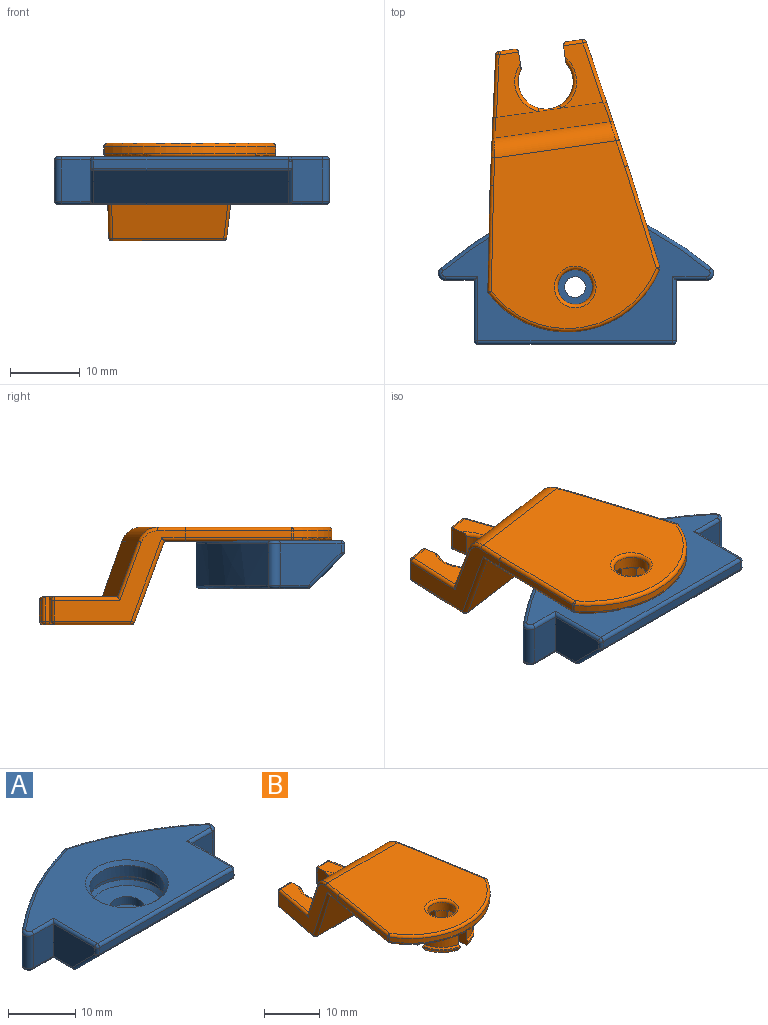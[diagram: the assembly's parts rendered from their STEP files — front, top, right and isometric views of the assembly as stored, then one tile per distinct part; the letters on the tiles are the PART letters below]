
ASSEMBLY  parts=2 mates=1
PART A: 51 faces, bbox 40.5x21.6x6.9 mm
  f0: cylinder r=2.5mm len=5mm, axis (0,0,1), area 22mm2, adj f12,f46
  f1: cylinder r=1.5mm len=3mm, axis (0,0,-1), area 8.5mm2, adj f12,f44
  f2: plane 8.72x5.9mm, normal (1,0,0), area 40.4mm2, adj f3,f23,f28,f34,f39
  f3: plane 5.9x4.38mm, normal (0,-1,0), area 25.8mm2, adj f2,f13,f21,f41
  f4: extruded ~19.54x10.36mm, area 131.4mm2, adj f5,f13,f17,f42
  f5: extruded ~19.28x10.34mm, area 130.1mm2, adj f4,f14,f15,f40
  f6: plane 5.9x4.15mm, normal (0,-1,0), area 24.5mm2, adj f7,f14,f18,f36
  f7: plane 8.72x5.9mm, normal (-1,0,0), area 40.4mm2, adj f6,f20,f25,f30,f33
  f8: plane 28x1.19mm, normal (0,-1,0), area 33.4mm2, adj f29,f30,f34,f35
  f9: plane 38.53x20.32mm, normal (0,0,1), area 401.7mm2, adj f33,f35,f36,f38,f39,f40,f41,f42
  f10: plane 38.53x15.61mm, normal (0,0,-1), area 376.2mm2, adj f15,f16,f17,f18,f19,f20,f21,f23
  f11: plane 28x4.71mm, normal (0,-0.71,-0.71), area 186.4mm2, adj f24,f25,f28,f29
  f12: plane 5x5mm, normal (0,0,1), area 12.6mm2, adj f0,f1
  f13: cylinder r=1mm len=5.9mm, axis (0,0,-1), area 14.3mm2, adj f3,f4,f19,f43
  f14: cylinder r=1mm len=5.9mm, axis (0,0,-1), area 14.5mm2, adj f5,f6,f16,f38
  f15: bspline ~20.66x11.54mm, area 17.2mm2, adj f5,f10,f16,f17
  f16: torus R=0.5mm, axis (0,0,1), area 1.6mm2, adj f10,f14,f15,f18
  f17: bspline ~21.54x11.77mm, area 17.4mm2, adj f4,f10,f15,f19
  f18: cylinder r=0.5mm len=4.65mm, axis (1,0,0), area 3.5mm2, adj f6,f10,f16,f20
  f19: torus R=0.5mm, axis (0,0,1), area 1.6mm2, adj f10,f13,f17,f21
  f20: cylinder r=0.5mm len=4.51mm, axis (0,-1,0), area 3.3mm2, adj f7,f10,f18,f22
  f21: cylinder r=0.5mm len=4.88mm, axis (1,0,0), area 3.6mm2, adj f3,f10,f19,f23
  f22: sphere r=0.5mm, area 0.1mm2, adj f20,f24,f25
  f23: cylinder r=0.5mm len=4.51mm, axis (0,1,0), area 3.3mm2, adj f2,f10,f21,f26
  f24: cylinder r=0.5mm len=28mm, axis (1,0,0), area 11mm2, adj f10,f11,f22,f26
  f25: cylinder r=0.5mm len=5.06mm, axis (0,-0.71,0.71), area 5.2mm2, adj f7,f11,f22,f27
  f26: sphere r=0.5mm, area 0.2mm2, adj f23,f24,f28
  f27: sphere r=0.5mm, area 0.2mm2, adj f25,f29,f30
  f28: cylinder r=0.5mm len=5.06mm, axis (0,0.71,-0.71), area 5.2mm2, adj f2,f11,f26,f31
  f29: cylinder r=0.5mm len=28mm, axis (1,0,0), area 11mm2, adj f8,f11,f27,f31
  f30: cylinder r=0.5mm len=1.19mm, axis (0,0,-1), area 0.9mm2, adj f7,f8,f27,f32
  f31: sphere r=0.5mm, area 0.2mm2, adj f28,f29,f34
  f32: sphere r=0.5mm, area 0.4mm2, adj f30,f33,f35
  f33: cylinder r=0.5mm len=9.22mm, axis (0,1,0), area 7mm2, adj f7,f9,f32,f36
  f34: cylinder r=0.5mm len=1.19mm, axis (0,0,-1), area 0.9mm2, adj f2,f8,f31,f37
  f35: cylinder r=0.5mm len=28mm, axis (-1,0,0), area 22mm2, adj f8,f9,f32,f37
  f36: cylinder r=0.5mm len=4.65mm, axis (-1,0,0), area 3.5mm2, adj f6,f9,f33,f38
  f37: sphere r=0.5mm, area 0.5mm2, adj f34,f35,f39
  f38: torus R=0.5mm, axis (0,0,1), area 1.6mm2, adj f9,f14,f36,f40
  f39: cylinder r=0.5mm len=9.22mm, axis (0,-1,0), area 7mm2, adj f2,f9,f37,f41
  f40: bspline ~20.66x11.54mm, area 17.2mm2, adj f5,f9,f38,f42
  f41: cylinder r=0.5mm len=4.88mm, axis (-1,0,0), area 3.6mm2, adj f3,f9,f39,f43
  f42: bspline ~21.54x11.77mm, area 17.4mm2, adj f4,f9,f40,f43
  f43: torus R=0.5mm, axis (0,0,1), area 1.6mm2, adj f9,f13,f41,f42
  f44: torus R=2mm, axis (0,0,1), area 8.3mm2, adj f1,f10
  f45: cylinder r=5.55mm len=11.1mm, axis (0,0,1), area 69.7mm2, adj f49,f50
  f46: plane 10.7x10.7mm, normal (0,0,1), area 70.3mm2, adj f0,f48
  f47: cylinder r=5.85mm len=11.7mm, axis (0,0,1), area 17.9mm2, adj f48,f49
  f48: cone r=5.35mm half-angle=35deg, axis (0,0,1), area 30.7mm2, adj f46,f47
  f49: cone r=5.85mm half-angle=45deg, axis (0,0,-1), area 15.2mm2, adj f45,f47
  f50: cone r=5.55mm half-angle=45deg, axis (0,0,1), area 31.2mm2, adj f9,f45
PART B: 124 faces, bbox 27x42.8x14.2 mm
  f0: plane 3.44x1mm, normal (0,0,-1), area 3.4mm2, adj f13,f58,f62,f93
  f1: plane 8.86x6.05mm, normal (0,0,1), area 28.1mm2, adj f44,f49,f69,f71,f120
  f2: plane 24.89x23.96mm, normal (0,0,-1), area 393.8mm2, adj f13,f50,f51,f53,f54,f55,f57,f59
  f3: plane 18.45x13mm, normal (0.98,0.18,0), area 64.3mm2, adj f69,f70,f72,f73,f77,f79,f80,f82
  f4: plane 18.45x13mm, normal (-0.98,0.18,0), area 64.3mm2, adj f98,f99,f105,f110,f113,f116,f117,f118
  f5: plane 25.86x23.96mm, normal (0,0,1), area 483.9mm2, adj f67,f82,f91,f102,f112,f117,f123
  f6: cylinder r=5.5mm len=4.41mm, axis (0,0,1), area 14.6mm2, adj f26,f27,f35,f60
  f7: cylinder r=5.5mm len=4.41mm, axis (0,0,1), area 14.6mm2, adj f22,f23,f37,f57
  f8: cylinder r=5.5mm len=4.41mm, axis (0,0,1), area 14.6mm2, adj f18,f20,f36,f53
  f9: cylinder r=5.5mm len=4.41mm, axis (0,0,1), area 14.6mm2, adj f15,f16,f34,f63
  f10: plane 15.07x2.47mm, normal (-0.99,0.16,0), area 15.3mm2, adj f103,f104,f112,f113
  f11: cylinder r=14.31mm len=24.82mm, axis (0,0,-1), area 30mm2, adj f92,f93,f102,f103
  f12: plane 15.07x2.47mm, normal (0.99,0.16,0), area 15.3mm2, adj f83,f84,f91,f92
  f13: cylinder r=2.5mm len=5mm, axis (0,0,-1), area 26.2mm2, adj f0,f2,f51,f52,f54,f55,f56,f58
  f14: cylinder r=2.75mm len=3.5mm, axis (0,0,1), area 8mm2, adj f15,f16,f17,f66
  f15: plane 3.5x3.16mm, normal (0,-1,0), area 10.1mm2, adj f9,f14,f17,f30,f34,f39,f64
  f16: plane 3.5x3.16mm, normal (-1,0,0), area 10.1mm2, adj f9,f14,f17,f30,f34,f39,f65
  f17: plane 4.21x4.21mm, normal (0,0,-1), area 11mm2, adj f14,f15,f16,f39
  f18: plane 3.5x3.16mm, normal (0,-1,0), area 10.1mm2, adj f8,f19,f21,f31,f36,f41,f51
  f19: cylinder r=2.75mm len=3.5mm, axis (0,0,1), area 8mm2, adj f18,f20,f21,f52
  f20: plane 3.5x3.16mm, normal (1,0,0), area 10.1mm2, adj f8,f19,f21,f31,f36,f41,f54
  f21: plane 4.21x4.21mm, normal (0,0,-1), area 11mm2, adj f18,f19,f20,f41
  f22: plane 3.5x3.16mm, normal (0,1,0), area 10.1mm2, adj f7,f24,f25,f32,f37,f40,f55
  f23: plane 3.5x3.16mm, normal (1,0,0), area 10.1mm2, adj f7,f24,f25,f32,f37,f40,f58
  f24: cylinder r=2.75mm len=3.5mm, axis (0,0,1), area 8mm2, adj f22,f23,f25,f56
  f25: plane 4.21x4.21mm, normal (0,0,-1), area 11mm2, adj f22,f23,f24,f40
  f26: plane 3.5x3.16mm, normal (-1,0,0), area 10.1mm2, adj f6,f28,f29,f33,f35,f38,f62
  f27: plane 3.5x3.16mm, normal (0,1,0), area 10.1mm2, adj f6,f28,f29,f33,f35,f38,f59
  f28: cylinder r=2.75mm len=3.5mm, axis (0,0,1), area 8mm2, adj f26,f27,f29,f61
  f29: plane 4.21x4.21mm, normal (0,0,-1), area 11mm2, adj f26,f27,f28,f38
  f30: cylinder r=5.8mm len=4.71mm, axis (0,0,1), area 2mm2, adj f15,f16,f34,f39
  f31: cylinder r=5.8mm len=4.71mm, axis (0,0,1), area 2mm2, adj f18,f20,f36,f41
  f32: cylinder r=5.8mm len=4.71mm, axis (0,0,1), area 2mm2, adj f22,f23,f37,f40
  f33: cylinder r=5.8mm len=4.71mm, axis (0,0,1), area 2mm2, adj f26,f27,f35,f38
  f34: cone r=4.8mm half-angle=45deg, axis (0,0,-1), area 2.9mm2, adj f9,f15,f16,f30
  f35: cone r=4.8mm half-angle=45deg, axis (0,0,-1), area 2.9mm2, adj f6,f26,f27,f33
  f36: cone r=4.8mm half-angle=45deg, axis (0,0,-1), area 2.9mm2, adj f8,f18,f20,f31
  f37: cone r=4.8mm half-angle=45deg, axis (0,0,-1), area 2.9mm2, adj f7,f22,f23,f32
  f38: cone r=5.8mm half-angle=35deg, axis (0,0,1), area 5.8mm2, adj f26,f27,f29,f33
  f39: cone r=5.8mm half-angle=35deg, axis (0,0,1), area 5.8mm2, adj f15,f16,f17,f30
  f40: cone r=5.8mm half-angle=35deg, axis (0,0,1), area 5.8mm2, adj f22,f23,f25,f32
  f41: cone r=5.8mm half-angle=35deg, axis (0,0,1), area 5.8mm2, adj f18,f20,f21,f31
  f42: plane 16.17x10.78mm, normal (0,0,-1), area 83.9mm2, adj f75,f80,f86,f89,f90,f95,f99,f100
  f43: plane 3x2.33mm, normal (0,1,0), area 7mm2, adj f70,f71,f75,f76
  f44: plane 3.67x2.66mm, normal (-1,0,0), area 8.6mm2, adj f1,f45,f76,f86,f120
  f45: cylinder r=3.95mm len=7.9mm, axis (0,0,1), area 51.6mm2, adj f44,f46,f90,f120,f121,f122
  f46: plane 3.67x2.66mm, normal (1,0,0), area 8.6mm2, adj f45,f48,f95,f107,f122
  f47: plane 3x2.33mm, normal (0,1,0), area 7mm2, adj f100,f107,f110,f111
  f48: plane 8.86x6.05mm, normal (0,0,1), area 28.1mm2, adj f46,f49,f111,f116,f122
  f49: plane 16.75x8.07mm, normal (0,0.94,0.34), area 138.1mm2, adj f1,f48,f67,f69,f72,f116,f118,f121
  f50: plane 17.75x11.67mm, normal (0,-0.94,-0.34), area 210.6mm2, adj f2,f79,f89,f98
  f51: plane 3.62x0.52mm, normal (0,-0.71,-0.71), area 2.3mm2, adj f2,f13,f18,f52,f53
  f52: cone r=2.75mm half-angle=45deg, axis (0,0,-1), area 0.8mm2, adj f13,f19,f51,f54
  f53: cone r=6mm half-angle=45deg, axis (0,0,1), area 5.3mm2, adj f2,f8,f51,f54
  f54: plane 3.62x0.52mm, normal (0.71,0,-0.71), area 2.3mm2, adj f2,f13,f20,f52,f53
  f55: plane 3.62x0.52mm, normal (0,0.71,-0.71), area 2.3mm2, adj f2,f13,f22,f56,f57
  f56: cone r=2.75mm half-angle=45deg, axis (0,0,-1), area 0.8mm2, adj f13,f24,f55,f58
  f57: cone r=6mm half-angle=45deg, axis (0,0,1), area 5.3mm2, adj f2,f7,f55,f58,f93
  f58: plane 3.63x0.54mm, normal (0.71,0,-0.71), area 2.3mm2, adj f0,f13,f23,f56,f57,f93
  f59: plane 3.62x0.52mm, normal (0,0.71,-0.71), area 2.3mm2, adj f2,f13,f27,f60,f61
  f60: cone r=6mm half-angle=45deg, axis (0,0,1), area 5.3mm2, adj f2,f6,f59,f62,f93
  f61: cone r=2.75mm half-angle=45deg, axis (0,0,-1), area 0.8mm2, adj f13,f28,f59,f62
  f62: plane 3.63x0.54mm, normal (-0.71,0,-0.71), area 2.3mm2, adj f0,f13,f26,f60,f61,f93
  f63: cone r=6mm half-angle=45deg, axis (0,0,1), area 5.3mm2, adj f2,f9,f64,f65
  f64: plane 3.62x0.52mm, normal (0,-0.71,-0.71), area 2.3mm2, adj f2,f13,f15,f63,f66
  f65: plane 3.62x0.52mm, normal (-0.71,0,-0.71), area 2.3mm2, adj f2,f13,f16,f63,f66
  f66: cone r=2.75mm half-angle=45deg, axis (0,0,-1), area 0.8mm2, adj f13,f14,f64,f65
  f67: cylinder r=3mm len=17.59mm, axis (1,0,0), area 62.9mm2, adj f5,f49,f77,f119
  f68: sphere r=0.5mm, area 0.2mm2, adj f69,f70,f71
  f69: cylinder r=0.5mm len=9.3mm, axis (0.18,-0.98,0), area 7.2mm2, adj f1,f3,f49,f68,f72
  f70: cylinder r=0.5mm len=3mm, axis (0,0,-1), area 2.1mm2, adj f3,f43,f68,f74
  f71: cylinder r=0.5mm len=2.83mm, axis (-1,0,0), area 2mm2, adj f1,f43,f68,f76
  f72: cylinder r=0.5mm len=8.53mm, axis (0.06,-0.34,0.94), area 6.1mm2, adj f3,f49,f69,f77
  f73: cylinder r=0.5mm len=3.39mm, axis (-0.18,0.98,0), area 2.5mm2, adj f2,f3,f78,f79
  f74: sphere r=0.5mm, area 0.5mm2, adj f70,f75,f80
  f75: cylinder r=0.5mm len=2.33mm, axis (1,0,0), area 1.8mm2, adj f42,f43,f74,f81
  f76: cylinder r=0.5mm len=3.5mm, axis (0,0,1), area 2.6mm2, adj f43,f44,f71,f81
  f77: bspline ~3.46x2.46mm, area 2.5mm2, adj f3,f67,f72,f82
  f78: sphere r=0.5mm, area 0mm2, adj f73,f83,f84
  f79: cylinder r=0.5mm len=12.17mm, axis (0.06,-0.34,0.94), area 10.9mm2, adj f2,f3,f50,f73,f85
  f80: cylinder r=0.5mm len=10.87mm, axis (-0.18,0.98,0), area 8.6mm2, adj f3,f42,f74,f85
  f81: sphere r=0.5mm, area 0.4mm2, adj f75,f76,f86
  f82: cylinder r=0.5mm len=3.94mm, axis (0.18,-0.98,0), area 3.1mm2, adj f3,f5,f77,f87
  f83: cylinder r=0.5mm len=1mm, axis (0,0,-1), area 0mm2, adj f3,f12,f78,f87
  f84: cylinder r=0.5mm len=15.15mm, axis (-0.16,0.99,0), area 12mm2, adj f2,f12,f78,f88
  f85: sphere r=0.5mm, area 0.3mm2, adj f79,f80,f89
  f86: cylinder r=0.5mm len=2.49mm, axis (0,1,0), area 1.9mm2, adj f42,f44,f81,f90
  f87: sphere r=0.5mm, area 0mm2, adj f82,f83,f91
  f88: sphere r=0.5mm, area 0.2mm2, adj f84,f92,f93
  f89: cylinder r=0.5mm len=16.17mm, axis (-1,0,0), area 9.9mm2, adj f42,f50,f85,f94
  f90: torus R=4.45mm, axis (0,0,1), area 14mm2, adj f42,f45,f86,f95
  f91: cylinder r=0.5mm len=15.15mm, axis (0.16,-0.99,0), area 12mm2, adj f5,f12,f87,f96
  f92: cylinder r=0.5mm len=1mm, axis (0,0,-1), area 0.3mm2, adj f11,f12,f88,f96
  f93: torus R=13.81mm, axis (0,0,1), area 23.2mm2, adj f0,f2,f11,f57,f58,f60,f62,f88
  f94: sphere r=0.5mm, area 0.3mm2, adj f89,f98,f99
  f95: cylinder r=0.5mm len=2.49mm, axis (0,-1,0), area 1.9mm2, adj f42,f46,f90,f101
  f96: sphere r=0.5mm, area 0.2mm2, adj f91,f92,f102
  f97: sphere r=0.5mm, area 0.2mm2, adj f93,f103,f104
  f98: cylinder r=0.5mm len=12.17mm, axis (0.06,0.34,-0.94), area 10.9mm2, adj f2,f4,f50,f94,f105
  f99: cylinder r=0.5mm len=10.87mm, axis (-0.18,-0.98,0), area 8.6mm2, adj f4,f42,f94,f106
  f100: cylinder r=0.5mm len=2.33mm, axis (1,0,0), area 1.8mm2, adj f42,f47,f101,f106
  f101: sphere r=0.5mm, area 0.5mm2, adj f95,f100,f107
  f102: torus R=13.81mm, axis (0,0,1), area 23.3mm2, adj f5,f11,f96,f108
  f103: cylinder r=0.5mm len=1mm, axis (0,0,-1), area 0.3mm2, adj f10,f11,f97,f108
  f104: cylinder r=0.5mm len=15.15mm, axis (-0.16,-0.99,0), area 12mm2, adj f2,f10,f97,f109
  f105: cylinder r=0.5mm len=3.39mm, axis (-0.18,-0.98,0), area 2.5mm2, adj f2,f4,f98,f109
  f106: sphere r=0.5mm, area 0.5mm2, adj f99,f100,f110
  f107: cylinder r=0.5mm len=3.5mm, axis (0,0,-1), area 2.6mm2, adj f46,f47,f101,f111
  f108: sphere r=0.5mm, area 0.2mm2, adj f102,f103,f112
  f109: sphere r=0.5mm, area 0mm2, adj f104,f105,f113
  f110: cylinder r=0.5mm len=3mm, axis (0,0,-1), area 2.1mm2, adj f4,f47,f106,f114
  f111: cylinder r=0.5mm len=2.83mm, axis (-1,0,0), area 2mm2, adj f47,f48,f107,f114
  f112: cylinder r=0.5mm len=15.15mm, axis (0.16,0.99,0), area 12mm2, adj f5,f10,f108,f115
  f113: cylinder r=0.5mm len=1mm, axis (0,0,-1), area 0mm2, adj f4,f10,f109,f115
  f114: sphere r=0.5mm, area 0.5mm2, adj f110,f111,f116
  f115: sphere r=0.5mm, area 0mm2, adj f112,f113,f117
  f116: cylinder r=0.5mm len=9.3mm, axis (0.18,0.98,0), area 7.2mm2, adj f4,f48,f49,f114,f118
  f117: cylinder r=0.5mm len=3.94mm, axis (0.18,0.98,0), area 3.1mm2, adj f4,f5,f115,f119
  f118: cylinder r=0.5mm len=8.53mm, axis (0.06,0.34,-0.94), area 6.1mm2, adj f4,f49,f116,f119
  f119: bspline ~3.07x2.46mm, area 2.5mm2, adj f4,f67,f117,f118
  f120: torus R=4.45mm, axis (0,0,1), area 6.1mm2, adj f1,f44,f45,f121
  f121: bspline ~3.9x0.67mm, area 1.7mm2, adj f45,f49,f120,f122
  f122: torus R=4.45mm, axis (0,0,1), area 6.1mm2, adj f45,f46,f48,f121
  f123: torus R=3mm, axis (0,0,1), area 13.2mm2, adj f5,f13
PLACE A t=(-5.08,-2.16,1.23)mm fixed
PLACE B rot(axis=(0,0,1),8.1deg) t=(-0.52,-34.34,1.13)mm
MATE revolute A.f0 <-> B.f6  axis (0,0,1) through (-5.08,-2.16,4.03)mm
